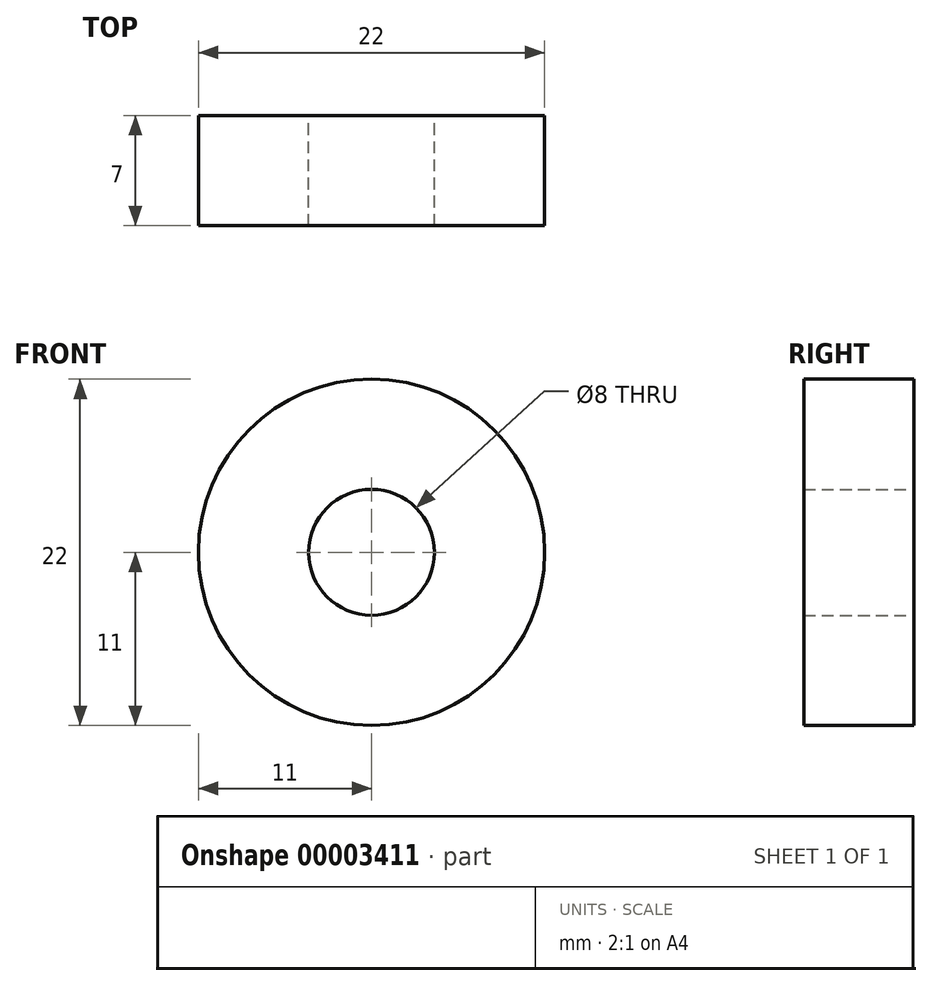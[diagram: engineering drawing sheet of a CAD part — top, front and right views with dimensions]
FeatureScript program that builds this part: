
annotation { "Feature Type Name" : "Feature", "Feature Type Description" : "" }
export const myFeature = defineFeature(function(context is Context, id is Id, definition is map)
    precondition{}
    {
        {
            var Q0;
            Q0=qCreatedBy(makeId("Front.planeOp"),FACE);
            var sketch = newSketch(context, id + "F0", { "sketchPlane" : qUnion([Q0])});
            skCircle(sketch, "E0", {"center": v(0, 0) * mm, "radius": 11 * mm});
            skCircle(sketch, "E1", {"center": v(0, 0) * mm, "radius": 4 * mm});
            skSolve(sketch);
        }
        {
            var Q0;
            Q0=makeQuery(id+"F0.imprint","IMPRINT",FACE,{"disambiguationData":[TD([[makeQuery(id+"F0.imprint","IMPRINT",EDGE,{"derivedFrom":sQuery(id+"F0.wireOp",EDGE,"E0")}),1.0]])]});
            extrude(context, id + "F1", {"entities" : qUnion([Q0]), "depth" : 7 * mm});
        }
    });
